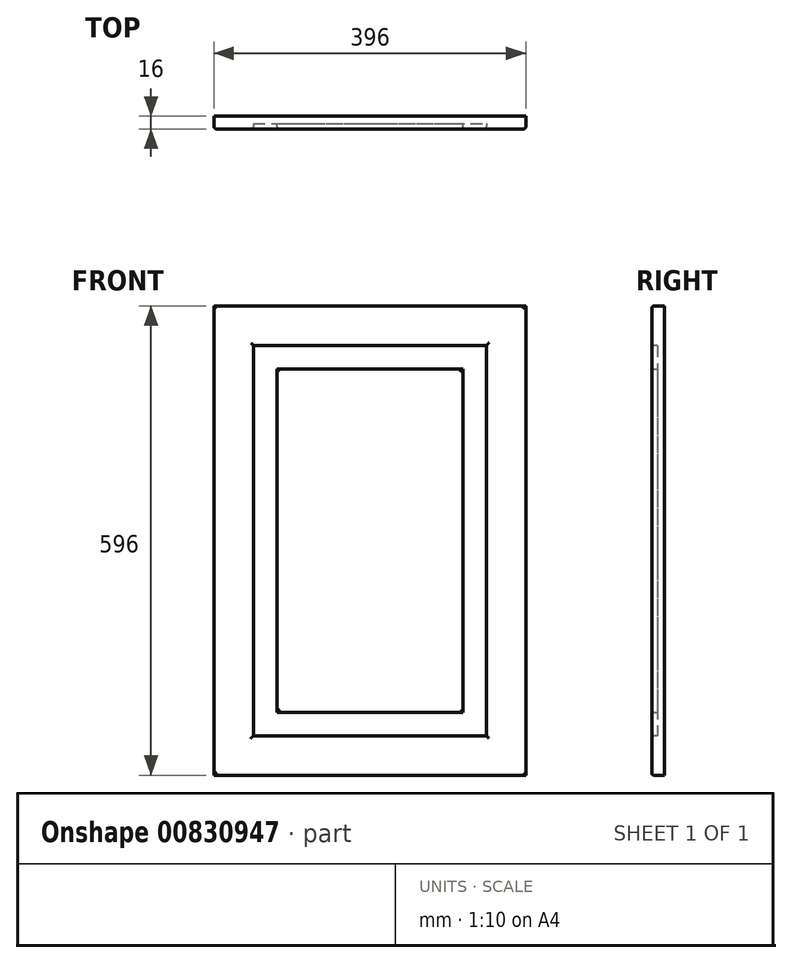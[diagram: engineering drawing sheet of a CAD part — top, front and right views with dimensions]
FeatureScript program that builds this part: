
annotation { "Feature Type Name" : "Feature", "Feature Type Description" : "" }
export const myFeature = defineFeature(function(context is Context, id is Id, definition is map)
    precondition{}
    {
        {
            var Q0;
            Q0=qCreatedBy(makeId("Front.planeOp"),FACE);
            var sketch = newSketch(context, id + "F0", { "sketchPlane" : qUnion([Q0])});
            skLineSegment(sketch, "E0.bottom", {"start": v(0, 0) * mm, "end": v(44.66, 0) * mm});
            skLineSegment(sketch, "E0.top", {"start": v(0, 33.8) * mm, "end": v(44.66, 33.8) * mm});
            skLineSegment(sketch, "E0.left", {"start": v(0, 0) * mm, "end": v(0, 33.8) * mm});
            skLineSegment(sketch, "E0.right", {"start": v(44.66, 0) * mm, "end": v(44.66, 33.8) * mm});
            skSolve(sketch);
        }
        {
            var Q0;
            Q0=makeQuery(id+"F0.imprint","IMPRINT",FACE,{"disambiguationData":[TD([[makeQuery(id+"F0.imprint","IMPRINT",EDGE,{"derivedFrom":sQuery(id+"F0.wireOp",EDGE,"E0.bottom")}),1.0]])]});
            extrude(context, id + "F1", {"entities" : qUnion([Q0]), "depth" : 16 * mm, "offsetDistance" : 25.4 * mm});
        }
        {
            var Q0;
            Q0=makeQuery(id+"F1.opExtrude","SWEPT_FACE",FACE,{"disambiguationData":[OSD([sQuery(id+"F0.wireOp",EDGE,"E0.bottom")])]});
            extrude(context, id + "F2", {"entities" : qUnion([Q0]), "operationType" : NewBodyOperationType.ADD, "oppositeDirection" : true, "depth" : 796 * mm, "offsetDistance" : 25 * mm});
        }
        {
            var Q0;
            {var subQ0=sQuery(id+"F0.wireOp",EDGE,"E0.left");Q0=makeQuery(id+"F2.boolean.opBoolean","MERGE",FACE,{"derivedFrom":[makeQuery(id+"F1.opExtrude","SWEPT_FACE",FACE,{"disambiguationData":[OSD([subQ0])]}),makeQuery(id+"F2.opExtrude","SWEPT_FACE",FACE,{"disambiguationData":[OSD([sQuery(id+"F0.wireOp",EDGE,"E0.bottom"),subQ0])]})]});}
            extrude(context, id + "F3", {"entities" : qUnion([Q0]), "operationType" : NewBodyOperationType.ADD, "oppositeDirection" : true, "depth" : 196 * mm, "offsetDistance" : 25 * mm});
        }
        {
            var Q0;
            {var subQ0=sQuery(id+"F0.wireOp",EDGE,"E0.left");var subQ1=sQuery(id+"F0.wireOp",EDGE,"E0.bottom");Q0=makeQuery(id+"F3.boolean.opBoolean","MERGE",FACE,{"derivedFrom":[makeQuery(id+"F2.boolean.opBoolean","MERGE",FACE,{"derivedFrom":[makeQuery(id+"F1.opExtrude","CAP_FACE",FACE,{"disambiguationData":[OSD([subQ1,sQuery(id+"F0.wireOp",EDGE,"E0.top"),subQ0,sQuery(id+"F0.wireOp",EDGE,"E0.right")])],"isStart":false}),makeQuery(id+"F2.opExtrude","SWEPT_FACE",FACE,{"disambiguationData":[OSD([subQ1]),TDD([makeQuery(id+"F1.opExtrude","CAP_EDGE",EDGE,{"disambiguationData":[OSD([subQ1])],"isStart":false})])]})]}),makeQuery(id+"F3.opExtrude","SWEPT_FACE",FACE,{"disambiguationData":[OSD([subQ1,subQ0]),TDD([makeQuery(id+"F2.boolean.opBoolean","MERGE",EDGE,{"derivedFrom":[makeQuery(id+"F1.opExtrude","CAP_EDGE",EDGE,{"disambiguationData":[OSD([subQ0])],"isStart":false}),makeQuery(id+"F2.opExtrude","SWEPT_EDGE",EDGE,{"disambiguationData":[OSD([subQ1,subQ0]),TDD([makeQuery(id+"F1.opExtrude","CAP_VERTEX",VERTEX,{"disambiguationData":[OSD([subQ1,subQ0])],"isStart":false})])]})]})])]})]});}
            var sketch = newSketch(context, id + "F4", { "sketchPlane" : qUnion([Q0])});
            skLineSegment(sketch, "E1.bottom", {"start": v(59.7, 646.67) * mm, "end": v(128.66, 646.67) * mm});
            skLineSegment(sketch, "E1.top", {"start": v(59.7, 152.97) * mm, "end": v(128.66, 152.97) * mm});
            skLineSegment(sketch, "E1.left", {"start": v(59.7, 646.67) * mm, "end": v(59.7, 152.97) * mm});
            skLineSegment(sketch, "E1.right", {"start": v(128.66, 646.67) * mm, "end": v(128.66, 152.97) * mm});
            skSolve(sketch);
        }
        {
            var Q0;
            Q0=makeQuery(id+"F4.imprint","IMPRINT",FACE,{"disambiguationData":[TD([[makeQuery(id+"F4.imprint","IMPRINT",EDGE,{"derivedFrom":sQuery(id+"F4.wireOp",EDGE,"E1.bottom")}),-1.0]])]});
            extrude(context, id + "F5", {"entities" : qUnion([Q0]), "operationType" : NewBodyOperationType.REMOVE, "oppositeDirection" : true, "depth" : 7 * mm, "offsetDistance" : 25 * mm});
        }
        {
            var Q0;
            Q0=makeQuery(id+"F5.boolean.opBoolean","COPY",FACE,{"derivedFrom":makeQuery(id+"F5.opExtrude","SWEPT_FACE",FACE,{"disambiguationData":[OSD([sQuery(id+"F4.wireOp",EDGE,"E1.left")])]})});
            extrude(context, id + "F6", {"entities" : qUnion([Q0]), "operationType" : NewBodyOperationType.REMOVE, "oppositeDirection" : true, "depth" : 9.7 * mm, "offsetDistance" : 25 * mm});
        }
        {
            var Q0;
            {var subQ0=sQuery(id+"F4.wireOp",EDGE,"E1.bottom");Q0=makeQuery(id+"F6.boolean.opBoolean","MERGE",FACE,{"derivedFrom":[makeQuery(id+"F5.boolean.opBoolean","COPY",FACE,{"derivedFrom":makeQuery(id+"F5.opExtrude","SWEPT_FACE",FACE,{"disambiguationData":[OSD([subQ0])]})}),makeQuery(id+"F6.opExtrude","SWEPT_FACE",FACE,{"disambiguationData":[OSD([subQ0,sQuery(id+"F4.wireOp",EDGE,"E1.left")])]})]});}
            extrude(context, id + "F7", {"entities" : qUnion([Q0]), "operationType" : NewBodyOperationType.ADD, "oppositeDirection" : true, "depth" : 99.33 * mm, "offsetDistance" : 25 * mm});
        }
        {
            var Q0;
            {var subQ0=sQuery(id+"F4.wireOp",EDGE,"E1.bottom");Q0=makeQuery(id+"F6.boolean.opBoolean","MERGE",FACE,{"derivedFrom":[makeQuery(id+"F5.boolean.opBoolean","COPY",FACE,{"derivedFrom":makeQuery(id+"F5.opExtrude","SWEPT_FACE",FACE,{"disambiguationData":[OSD([subQ0])]})}),makeQuery(id+"F6.opExtrude","SWEPT_FACE",FACE,{"disambiguationData":[OSD([subQ0,sQuery(id+"F4.wireOp",EDGE,"E1.left")])]})]});}
            extrude(context, id + "F8", {"entities" : qUnion([Q0]), "operationType" : NewBodyOperationType.REMOVE, "oppositeDirection" : true, "depth" : 99.33 * mm, "offsetDistance" : 25 * mm});
        }
        {
            var Q0;
            {var subQ0=sQuery(id+"F4.wireOp",EDGE,"E1.right");Q0=makeQuery(id+"F8.boolean.opBoolean","MERGE",FACE,{"derivedFrom":[makeQuery(id+"F5.boolean.opBoolean","COPY",FACE,{"derivedFrom":makeQuery(id+"F5.opExtrude","SWEPT_FACE",FACE,{"disambiguationData":[OSD([subQ0])]})}),makeQuery(id+"F8.opExtrude","SWEPT_FACE",FACE,{"disambiguationData":[OSD([sQuery(id+"F4.wireOp",EDGE,"E1.bottom"),subQ0])]})]});}
            extrude(context, id + "F9", {"entities" : qUnion([Q0]), "operationType" : NewBodyOperationType.REMOVE, "oppositeDirection" : true, "depth" : 17.34 * mm, "offsetDistance" : 25 * mm});
        }
        {
            var Q0;
            {var subQ0=sQuery(id+"F4.wireOp",EDGE,"E1.top");Q0=makeQuery(id+"F9.boolean.opBoolean","MERGE",FACE,{"derivedFrom":[makeQuery(id+"F6.boolean.opBoolean","MERGE",FACE,{"derivedFrom":[makeQuery(id+"F5.boolean.opBoolean","COPY",FACE,{"derivedFrom":makeQuery(id+"F5.opExtrude","SWEPT_FACE",FACE,{"disambiguationData":[OSD([subQ0])]})}),makeQuery(id+"F6.opExtrude","SWEPT_FACE",FACE,{"disambiguationData":[OSD([subQ0,sQuery(id+"F4.wireOp",EDGE,"E1.left")])]})]}),makeQuery(id+"F9.opExtrude","SWEPT_FACE",FACE,{"disambiguationData":[OSD([subQ0,sQuery(id+"F4.wireOp",EDGE,"E1.right")])]})]});}
            extrude(context, id + "F10", {"entities" : qUnion([Q0]), "operationType" : NewBodyOperationType.REMOVE, "oppositeDirection" : true, "depth" : 102.97 * mm, "offsetDistance" : 25 * mm});
        }
        {
            var Q0;
            {var subQ0=sQuery(id+"F4.wireOp",EDGE,"E1.right");var subQ1=sQuery(id+"F4.wireOp",EDGE,"E1.top");var subQ2=sQuery(id+"F4.wireOp",EDGE,"E1.left");var subQ3=sQuery(id+"F4.wireOp",EDGE,"E1.bottom");Q0=makeQuery(id+"F10.boolean.opBoolean","MERGE",FACE,{"derivedFrom":[makeQuery(id+"F9.boolean.opBoolean","MERGE",FACE,{"derivedFrom":[makeQuery(id+"F8.boolean.opBoolean","MERGE",FACE,{"derivedFrom":[makeQuery(id+"F6.boolean.opBoolean","MERGE",FACE,{"derivedFrom":[makeQuery(id+"F5.boolean.opBoolean","COPY",FACE,{"derivedFrom":makeQuery(id+"F5.opExtrude","CAP_FACE",FACE,{"disambiguationData":[OSD([subQ3,subQ1,subQ2,subQ0])],"isStart":false})}),makeQuery(id+"F6.opExtrude","SWEPT_FACE",FACE,{"disambiguationData":[OSD([subQ2]),TDD([makeQuery(id+"F5.boolean.opBoolean","COPY",EDGE,{"derivedFrom":makeQuery(id+"F5.opExtrude","CAP_EDGE",EDGE,{"disambiguationData":[OSD([subQ2])],"isStart":false})})])]})]}),makeQuery(id+"F8.opExtrude","SWEPT_FACE",FACE,{"disambiguationData":[OSD([subQ3,subQ2]),TDD([makeQuery(id+"F6.boolean.opBoolean","MERGE",EDGE,{"derivedFrom":[makeQuery(id+"F5.boolean.opBoolean","COPY",EDGE,{"derivedFrom":makeQuery(id+"F5.opExtrude","CAP_EDGE",EDGE,{"disambiguationData":[OSD([subQ3])],"isStart":false})}),makeQuery(id+"F6.opExtrude","SWEPT_EDGE",EDGE,{"disambiguationData":[OSD([subQ3,subQ2]),TDD([makeQuery(id+"F5.boolean.opBoolean","COPY",VERTEX,{"derivedFrom":makeQuery(id+"F5.opExtrude","CAP_VERTEX",VERTEX,{"disambiguationData":[OSD([subQ3,subQ2])],"isStart":false})})])]})]})])]})]}),makeQuery(id+"F9.opExtrude","SWEPT_FACE",FACE,{"disambiguationData":[OSD([subQ3,subQ0]),TDD([makeQuery(id+"F8.boolean.opBoolean","MERGE",EDGE,{"derivedFrom":[makeQuery(id+"F5.boolean.opBoolean","COPY",EDGE,{"derivedFrom":makeQuery(id+"F5.opExtrude","CAP_EDGE",EDGE,{"disambiguationData":[OSD([subQ0])],"isStart":false})}),makeQuery(id+"F8.opExtrude","SWEPT_EDGE",EDGE,{"disambiguationData":[OSD([subQ3,subQ0]),TDD([makeQuery(id+"F5.boolean.opBoolean","COPY",VERTEX,{"derivedFrom":makeQuery(id+"F5.opExtrude","CAP_VERTEX",VERTEX,{"disambiguationData":[OSD([subQ3,subQ0])],"isStart":false})})])]})]})])]})]}),makeQuery(id+"F10.opExtrude","SWEPT_FACE",FACE,{"disambiguationData":[OSD([subQ1,subQ2,subQ0]),TDD([makeQuery(id+"F9.boolean.opBoolean","MERGE",EDGE,{"derivedFrom":[makeQuery(id+"F6.boolean.opBoolean","MERGE",EDGE,{"derivedFrom":[makeQuery(id+"F5.boolean.opBoolean","COPY",EDGE,{"derivedFrom":makeQuery(id+"F5.opExtrude","CAP_EDGE",EDGE,{"disambiguationData":[OSD([subQ1])],"isStart":false})}),makeQuery(id+"F6.opExtrude","SWEPT_EDGE",EDGE,{"disambiguationData":[OSD([subQ1,subQ2]),TDD([makeQuery(id+"F5.boolean.opBoolean","COPY",VERTEX,{"derivedFrom":makeQuery(id+"F5.opExtrude","CAP_VERTEX",VERTEX,{"disambiguationData":[OSD([subQ1,subQ2])],"isStart":false})})])]})]}),makeQuery(id+"F9.opExtrude","SWEPT_EDGE",EDGE,{"disambiguationData":[OSD([subQ1,subQ0]),TDD([makeQuery(id+"F5.boolean.opBoolean","COPY",VERTEX,{"derivedFrom":makeQuery(id+"F5.opExtrude","CAP_VERTEX",VERTEX,{"disambiguationData":[OSD([subQ1,subQ0])],"isStart":false})})])]})]})])]})]});}
            var sketch = newSketch(context, id + "F11", { "sketchPlane" : qUnion([Q0])});
            skLineSegment(sketch, "E2.bottom", {"start": v(74.13, 678.73) * mm, "end": v(109.41, 678.73) * mm});
            skLineSegment(sketch, "E2.top", {"start": v(74.13, 186.63) * mm, "end": v(109.41, 186.63) * mm});
            skLineSegment(sketch, "E2.left", {"start": v(74.13, 678.73) * mm, "end": v(74.13, 186.63) * mm});
            skLineSegment(sketch, "E2.right", {"start": v(109.41, 678.73) * mm, "end": v(109.41, 186.63) * mm});
            skSolve(sketch);
        }
        {
            var Q0;
            Q0=makeQuery(id+"F11.imprint","IMPRINT",FACE,{"disambiguationData":[TD([[makeQuery(id+"F11.imprint","IMPRINT",EDGE,{"derivedFrom":sQuery(id+"F11.wireOp",EDGE,"E2.bottom")}),-1.0]])]});
            extrude(context, id + "F12", {"entities" : qUnion([Q0]), "operationType" : NewBodyOperationType.ADD, "depth" : 7 * mm, "offsetDistance" : 25 * mm});
        }
        {
            var Q0;
            Q0=makeQuery(id+"F12.opExtrude","SWEPT_FACE",FACE,{"disambiguationData":[OSD([sQuery(id+"F11.wireOp",EDGE,"E2.bottom")])]});
            extrude(context, id + "F13", {"entities" : qUnion([Q0]), "operationType" : NewBodyOperationType.ADD, "depth" : 37.27 * mm, "offsetDistance" : 25 * mm});
        }
        {
            var Q0;
            {var subQ0=sQuery(id+"F11.wireOp",EDGE,"E2.right");Q0=makeQuery(id+"F13.boolean.opBoolean","MERGE",FACE,{"derivedFrom":[makeQuery(id+"F12.opExtrude","SWEPT_FACE",FACE,{"disambiguationData":[OSD([subQ0])]}),makeQuery(id+"F13.opExtrude","SWEPT_FACE",FACE,{"disambiguationData":[OSD([sQuery(id+"F11.wireOp",EDGE,"E2.bottom"),subQ0])]})]});}
            extrude(context, id + "F14", {"entities" : qUnion([Q0]), "operationType" : NewBodyOperationType.ADD, "depth" : 6.58 * mm, "offsetDistance" : 25 * mm});
        }
        {
            var Q0;
            {var subQ0=sQuery(id+"F11.wireOp",EDGE,"E2.top");Q0=makeQuery(id+"F14.boolean.opBoolean","MERGE",FACE,{"derivedFrom":[makeQuery(id+"F12.opExtrude","SWEPT_FACE",FACE,{"disambiguationData":[OSD([subQ0])]}),makeQuery(id+"F14.opExtrude","SWEPT_FACE",FACE,{"disambiguationData":[OSD([subQ0,sQuery(id+"F11.wireOp",EDGE,"E2.right")])]})]});}
            extrude(context, id + "F15", {"entities" : qUnion([Q0]), "operationType" : NewBodyOperationType.ADD, "depth" : 106.63 * mm, "offsetDistance" : 25 * mm});
        }
        {
            var Q0;
            {var subQ0=sQuery(id+"F11.wireOp",EDGE,"E2.left");Q0=makeQuery(id+"F15.boolean.opBoolean","MERGE",FACE,{"derivedFrom":[makeQuery(id+"F13.boolean.opBoolean","MERGE",FACE,{"derivedFrom":[makeQuery(id+"F12.opExtrude","SWEPT_FACE",FACE,{"disambiguationData":[OSD([subQ0])]}),makeQuery(id+"F13.opExtrude","SWEPT_FACE",FACE,{"disambiguationData":[OSD([sQuery(id+"F11.wireOp",EDGE,"E2.bottom"),subQ0])]})]}),makeQuery(id+"F15.opExtrude","SWEPT_FACE",FACE,{"disambiguationData":[OSD([sQuery(id+"F11.wireOp",EDGE,"E2.top"),subQ0])]})]});}
            extrude(context, id + "F16", {"entities" : qUnion([Q0]), "operationType" : NewBodyOperationType.REMOVE, "oppositeDirection" : true, "depth" : 5.87 * mm, "offsetDistance" : 25 * mm});
        }
        {
            var Q0;
            Q0=makeQuery(id+"F3.opExtrude","CAP_FACE",FACE,{"disambiguationData":[OSD([sQuery(id+"F0.wireOp",EDGE,"E0.bottom"),sQuery(id+"F0.wireOp",EDGE,"E0.left")])],"isStart":false});
            extrude(context, id + "F17", {"entities" : qUnion([Q0]), "operationType" : NewBodyOperationType.ADD, "depth" : 200 * mm, "offsetDistance" : 25 * mm});
        }
        {
            var Q0;
            {var subQ0=sQuery(id+"F4.wireOp",EDGE,"E1.right");Q0=makeQuery(id+"F10.boolean.opBoolean","MERGE",FACE,{"derivedFrom":[makeQuery(id+"F9.boolean.opBoolean","COPY",FACE,{"derivedFrom":makeQuery(id+"F9.opExtrude","CAP_FACE",FACE,{"disambiguationData":[OSD([sQuery(id+"F4.wireOp",EDGE,"E1.bottom"),subQ0])],"isStart":false})}),makeQuery(id+"F10.opExtrude","SWEPT_FACE",FACE,{"disambiguationData":[OSD([sQuery(id+"F4.wireOp",EDGE,"E1.top"),subQ0])]})]});}
            extrude(context, id + "F18", {"entities" : qUnion([Q0]), "operationType" : NewBodyOperationType.REMOVE, "oppositeDirection" : true, "depth" : 200 * mm, "offsetDistance" : 25 * mm});
        }
        {
            var Q0;
            {var subQ0=sQuery(id+"F11.wireOp",EDGE,"E2.right");var subQ1=sQuery(id+"F11.wireOp",EDGE,"E2.top");Q0=makeQuery(id+"F15.boolean.opBoolean","MERGE",FACE,{"derivedFrom":[makeQuery(id+"F14.opExtrude","CAP_FACE",FACE,{"disambiguationData":[OSD([sQuery(id+"F11.wireOp",EDGE,"E2.bottom"),subQ0])],"isStart":false}),makeQuery(id+"F15.opExtrude","SWEPT_FACE",FACE,{"disambiguationData":[OSD([subQ1,subQ0]),TDD([makeQuery(id+"F14.opExtrude","CAP_EDGE",EDGE,{"disambiguationData":[OSD([subQ1,subQ0])],"isStart":false})])]})]});}
            extrude(context, id + "F19", {"entities" : qUnion([Q0]), "operationType" : NewBodyOperationType.ADD, "depth" : 200 * mm, "offsetDistance" : 25 * mm});
        }
        {
            var Q0;
            {var subQ0=sQuery(id+"F11.wireOp",EDGE,"E2.right");var subQ1=sQuery(id+"F11.wireOp",EDGE,"E2.top");Q0=makeQuery(id+"F19.boolean.opBoolean","MERGE",FACE,{"derivedFrom":[makeQuery(id+"F15.opExtrude","CAP_FACE",FACE,{"disambiguationData":[OSD([subQ1,subQ0])],"isStart":false}),makeQuery(id+"F19.opExtrude","SWEPT_FACE",FACE,{"disambiguationData":[OSD([subQ1,subQ0])]})]});}
            extrude(context, id + "F20", {"entities" : qUnion([Q0]), "operationType" : NewBodyOperationType.REMOVE, "oppositeDirection" : true, "depth" : 600 * mm, "offsetDistance" : 25 * mm});
        }
        {
            var Q0;
            {var subQ0=sQuery(id+"F4.wireOp",EDGE,"E1.right");var subQ1=sQuery(id+"F4.wireOp",EDGE,"E1.top");Q0=makeQuery(id+"F18.boolean.opBoolean","MERGE",FACE,{"derivedFrom":[makeQuery(id+"F10.boolean.opBoolean","COPY",FACE,{"derivedFrom":makeQuery(id+"F10.opExtrude","CAP_FACE",FACE,{"disambiguationData":[OSD([subQ1,sQuery(id+"F4.wireOp",EDGE,"E1.left"),subQ0])],"isStart":false})}),makeQuery(id+"F18.opExtrude","SWEPT_FACE",FACE,{"disambiguationData":[OSD([subQ1,subQ0])]})]});}
            extrude(context, id + "F21", {"entities" : qUnion([Q0]), "operationType" : NewBodyOperationType.ADD, "depth" : 600 * mm, "offsetDistance" : 25 * mm});
        }
        {
            var Q0;
            {var subQ0=sQuery(id+"F0.wireOp",EDGE,"E0.left");var subQ1=sQuery(id+"F0.wireOp",EDGE,"E0.bottom");var subQ2=makeQuery(id+"F1.opExtrude","SWEPT_EDGE",EDGE,{"disambiguationData":[OSD([subQ1,subQ0])]});Q0=makeQuery(id+"F17.boolean.opBoolean","MERGE",FACE,{"derivedFrom":[makeQuery(id+"F3.boolean.opBoolean","MERGE",FACE,{"derivedFrom":[makeQuery(id+"F1.opExtrude","SWEPT_FACE",FACE,{"disambiguationData":[OSD([subQ1])]}),makeQuery(id+"F3.opExtrude","SWEPT_FACE",FACE,{"disambiguationData":[OSD([subQ1,subQ0]),TDD([subQ2])]})]}),makeQuery(id+"F17.opExtrude","SWEPT_FACE",FACE,{"disambiguationData":[OSD([subQ1,subQ0]),TDD([makeQuery(id+"F3.opExtrude","CAP_EDGE",EDGE,{"disambiguationData":[OSD([subQ1,subQ0]),TDD([subQ2])],"isStart":false})])]})]});}
            extrude(context, id + "F22", {"entities" : qUnion([Q0]), "operationType" : NewBodyOperationType.REMOVE, "oppositeDirection" : true, "depth" : 600 * mm, "offsetDistance" : 25 * mm});
        }
        {
            var Q0;
            Q0=makeQuery(id+"F22.boolean.opBoolean","COPY",FACE,{"derivedFrom":makeQuery(id+"F22.opExtrude","CAP_FACE",FACE,{"disambiguationData":[OSD([sQuery(id+"F0.wireOp",EDGE,"E0.bottom"),sQuery(id+"F0.wireOp",EDGE,"E0.left")])],"isStart":false})});
            extrude(context, id + "F23", {"entities" : qUnion([Q0]), "operationType" : NewBodyOperationType.ADD, "depth" : 200 * mm, "offsetDistance" : 25 * mm});
        }
        {
            var Q0;
            Q0=makeQuery(id+"F21.opExtrude","CAP_FACE",FACE,{"disambiguationData":[OSD([sQuery(id+"F4.wireOp",EDGE,"E1.top"),sQuery(id+"F4.wireOp",EDGE,"E1.left"),sQuery(id+"F4.wireOp",EDGE,"E1.right")])],"isStart":false});
            extrude(context, id + "F24", {"entities" : qUnion([Q0]), "operationType" : NewBodyOperationType.REMOVE, "oppositeDirection" : true, "depth" : 200 * mm, "offsetDistance" : 25 * mm});
        }
        {
            var Q0;
            Q0=makeQuery(id+"F20.boolean.opBoolean","COPY",FACE,{"derivedFrom":makeQuery(id+"F20.opExtrude","CAP_FACE",FACE,{"disambiguationData":[OSD([sQuery(id+"F11.wireOp",EDGE,"E2.top"),sQuery(id+"F11.wireOp",EDGE,"E2.right")])],"isStart":false})});
            extrude(context, id + "F25", {"entities" : qUnion([Q0]), "operationType" : NewBodyOperationType.ADD, "depth" : 200 * mm, "offsetDistance" : 25 * mm});
        }
        {
            var Q0;
            {var subQ0=sQuery(id+"F0.wireOp",EDGE,"E0.left");var subQ1=sQuery(id+"F0.wireOp",EDGE,"E0.bottom");var subQ2=makeQuery(id+"F2.opExtrude","CAP_EDGE",EDGE,{"disambiguationData":[OSD([subQ1,subQ0])],"isStart":false});Q0=makeQuery(id+"F17.boolean.opBoolean","MERGE",FACE,{"derivedFrom":[makeQuery(id+"F3.boolean.opBoolean","MERGE",FACE,{"derivedFrom":[makeQuery(id+"F2.opExtrude","CAP_FACE",FACE,{"disambiguationData":[OSD([subQ1])],"isStart":false}),makeQuery(id+"F3.opExtrude","SWEPT_FACE",FACE,{"disambiguationData":[OSD([subQ1,subQ0]),TDD([subQ2])]})]}),makeQuery(id+"F17.opExtrude","SWEPT_FACE",FACE,{"disambiguationData":[OSD([subQ1,subQ0]),TDD([makeQuery(id+"F3.opExtrude","CAP_EDGE",EDGE,{"disambiguationData":[OSD([subQ1,subQ0]),TDD([subQ2])],"isStart":false})])]})]});}
            extrude(context, id + "F26", {"entities" : qUnion([Q0]), "operationType" : NewBodyOperationType.ADD, "depth" : 200 * mm, "offsetDistance" : 25 * mm});
        }
        {
            var Q0;
            {var subQ0=sQuery(id+"F4.wireOp",EDGE,"E1.right");var subQ1=sQuery(id+"F4.wireOp",EDGE,"E1.bottom");Q0=makeQuery(id+"F18.boolean.opBoolean","MERGE",FACE,{"derivedFrom":[makeQuery(id+"F9.boolean.opBoolean","MERGE",FACE,{"derivedFrom":[makeQuery(id+"F8.boolean.opBoolean","COPY",FACE,{"derivedFrom":makeQuery(id+"F8.opExtrude","CAP_FACE",FACE,{"disambiguationData":[OSD([subQ1,sQuery(id+"F4.wireOp",EDGE,"E1.left")])],"isStart":false})}),makeQuery(id+"F9.opExtrude","SWEPT_FACE",FACE,{"disambiguationData":[OSD([subQ1,subQ0]),TDD([makeQuery(id+"F8.boolean.opBoolean","COPY",EDGE,{"derivedFrom":makeQuery(id+"F8.opExtrude","CAP_EDGE",EDGE,{"disambiguationData":[OSD([subQ1,subQ0])],"isStart":false})})])]})]}),makeQuery(id+"F18.opExtrude","SWEPT_FACE",FACE,{"disambiguationData":[OSD([subQ1,subQ0])]})]});}
            extrude(context, id + "F27", {"entities" : qUnion([Q0]), "operationType" : NewBodyOperationType.REMOVE, "oppositeDirection" : true, "depth" : 200 * mm, "offsetDistance" : 25 * mm});
        }
        {
            var Q0;
            {var subQ0=sQuery(id+"F11.wireOp",EDGE,"E2.right");var subQ1=sQuery(id+"F11.wireOp",EDGE,"E2.bottom");Q0=makeQuery(id+"F19.boolean.opBoolean","MERGE",FACE,{"derivedFrom":[makeQuery(id+"F14.boolean.opBoolean","MERGE",FACE,{"derivedFrom":[makeQuery(id+"F13.opExtrude","CAP_FACE",FACE,{"disambiguationData":[OSD([subQ1])],"isStart":false}),makeQuery(id+"F14.opExtrude","SWEPT_FACE",FACE,{"disambiguationData":[OSD([subQ1,subQ0]),TDD([makeQuery(id+"F13.opExtrude","CAP_EDGE",EDGE,{"disambiguationData":[OSD([subQ1,subQ0])],"isStart":false})])]})]}),makeQuery(id+"F19.opExtrude","SWEPT_FACE",FACE,{"disambiguationData":[OSD([subQ1,subQ0])]})]});}
            extrude(context, id + "F28", {"entities" : qUnion([Q0]), "operationType" : NewBodyOperationType.ADD, "depth" : 200 * mm, "offsetDistance" : 25 * mm});
        }
        {
            var Q0;
            {var subQ0=sQuery(id+"F0.wireOp",EDGE,"E0.left");var subQ1=sQuery(id+"F0.wireOp",EDGE,"E0.bottom");var subQ2=makeQuery(id+"F1.opExtrude","CAP_VERTEX",VERTEX,{"disambiguationData":[OSD([subQ1,subQ0])],"isStart":false});var subQ3=makeQuery(id+"F2.opExtrude","CAP_VERTEX",VERTEX,{"disambiguationData":[OSD([subQ1,subQ0]),TDD([subQ2])],"isStart":false});var subQ4=makeQuery(id+"F1.opExtrude","CAP_EDGE",EDGE,{"disambiguationData":[OSD([subQ1])],"isStart":false});var subQ5=sQuery(id+"F4.wireOp",EDGE,"E1.right");var subQ6=sQuery(id+"F4.wireOp",EDGE,"E1.top");var subQ7=makeQuery(id+"F5.boolean.opBoolean","COPY",VERTEX,{"derivedFrom":makeQuery(id+"F5.opExtrude","CAP_VERTEX",VERTEX,{"disambiguationData":[OSD([subQ6,subQ5])],"isStart":true})});var subQ8=sQuery(id+"F4.wireOp",EDGE,"E1.left");var subQ9=makeQuery(id+"F2.boolean.opBoolean","MERGE",EDGE,{"derivedFrom":[makeQuery(id+"F1.opExtrude","CAP_EDGE",EDGE,{"disambiguationData":[OSD([subQ0])],"isStart":false}),makeQuery(id+"F2.opExtrude","SWEPT_EDGE",EDGE,{"disambiguationData":[OSD([subQ1,subQ0]),TDD([subQ2])]})]});Q0=makeQuery(id+"F26.boolean.opBoolean","MERGE",FACE,{"derivedFrom":[makeQuery(id+"F23.boolean.opBoolean","MERGE",FACE,{"derivedFrom":[makeQuery(id+"F21.boolean.opBoolean","MERGE",FACE,{"derivedFrom":[makeQuery(id+"F17.boolean.opBoolean","MERGE",FACE,{"derivedFrom":[makeQuery(id+"F3.boolean.opBoolean","MERGE",FACE,{"derivedFrom":[makeQuery(id+"F2.boolean.opBoolean","MERGE",FACE,{"derivedFrom":[makeQuery(id+"F1.opExtrude","CAP_FACE",FACE,{"disambiguationData":[OSD([subQ1,sQuery(id+"F0.wireOp",EDGE,"E0.top"),subQ0,sQuery(id+"F0.wireOp",EDGE,"E0.right")])],"isStart":false}),makeQuery(id+"F2.opExtrude","SWEPT_FACE",FACE,{"disambiguationData":[OSD([subQ1]),TDD([subQ4])]})]}),makeQuery(id+"F3.opExtrude","SWEPT_FACE",FACE,{"disambiguationData":[OSD([subQ1,subQ0]),TDD([subQ9])]})]}),makeQuery(id+"F17.opExtrude","SWEPT_FACE",FACE,{"disambiguationData":[OSD([subQ1,subQ0]),TDD([makeQuery(id+"F3.opExtrude","CAP_EDGE",EDGE,{"disambiguationData":[OSD([subQ1,subQ0]),TDD([subQ9])],"isStart":false})])]})]}),makeQuery(id+"F21.opExtrude","SWEPT_FACE",FACE,{"disambiguationData":[OSD([subQ6,subQ8,subQ5]),TDD([makeQuery(id+"F18.boolean.opBoolean","MERGE",EDGE,{"derivedFrom":[makeQuery(id+"F10.boolean.opBoolean","COPY",EDGE,{"derivedFrom":makeQuery(id+"F10.opExtrude","CAP_EDGE",EDGE,{"disambiguationData":[OSD([subQ6,subQ8,subQ5]),TDD([makeQuery(id+"F9.boolean.opBoolean","MERGE",EDGE,{"derivedFrom":[makeQuery(id+"F6.boolean.opBoolean","MERGE",EDGE,{"derivedFrom":[makeQuery(id+"F5.boolean.opBoolean","COPY",EDGE,{"derivedFrom":makeQuery(id+"F5.opExtrude","CAP_EDGE",EDGE,{"disambiguationData":[OSD([subQ6])],"isStart":true})}),makeQuery(id+"F6.opExtrude","SWEPT_EDGE",EDGE,{"disambiguationData":[OSD([subQ6,subQ8]),TDD([makeQuery(id+"F5.boolean.opBoolean","COPY",VERTEX,{"derivedFrom":makeQuery(id+"F5.opExtrude","CAP_VERTEX",VERTEX,{"disambiguationData":[OSD([subQ6,subQ8])],"isStart":true})})])]})]}),makeQuery(id+"F9.opExtrude","SWEPT_EDGE",EDGE,{"disambiguationData":[OSD([subQ6,subQ5]),TDD([subQ7])]})]})])],"isStart":false})}),makeQuery(id+"F18.opExtrude","SWEPT_EDGE",EDGE,{"disambiguationData":[OSD([subQ6,subQ5]),TDD([makeQuery(id+"F10.boolean.opBoolean","COPY",VERTEX,{"derivedFrom":makeQuery(id+"F10.opExtrude","CAP_VERTEX",VERTEX,{"disambiguationData":[OSD([subQ6,subQ5]),TDD([makeQuery(id+"F9.boolean.opBoolean","COPY",VERTEX,{"derivedFrom":makeQuery(id+"F9.opExtrude","CAP_VERTEX",VERTEX,{"disambiguationData":[OSD([subQ6,subQ5]),TDD([subQ7])],"isStart":false})})])],"isStart":false})})])]})]})])]})]}),makeQuery(id+"F23.opExtrude","SWEPT_FACE",FACE,{"disambiguationData":[OSD([subQ1,subQ0]),TDD([makeQuery(id+"F22.boolean.opBoolean","COPY",EDGE,{"derivedFrom":makeQuery(id+"F22.opExtrude","CAP_EDGE",EDGE,{"disambiguationData":[OSD([subQ1,subQ0]),TDD([makeQuery(id+"F17.boolean.opBoolean","MERGE",EDGE,{"derivedFrom":[makeQuery(id+"F3.boolean.opBoolean","MERGE",EDGE,{"derivedFrom":[subQ4,makeQuery(id+"F3.opExtrude","SWEPT_EDGE",EDGE,{"disambiguationData":[OSD([subQ1,subQ0]),TDD([subQ2])]})]}),makeQuery(id+"F17.opExtrude","SWEPT_EDGE",EDGE,{"disambiguationData":[OSD([subQ1,subQ0]),TDD([makeQuery(id+"F3.opExtrude","CAP_VERTEX",VERTEX,{"disambiguationData":[OSD([subQ1,subQ0]),TDD([subQ2])],"isStart":false})])]})]})])],"isStart":false})})])]})]}),makeQuery(id+"F26.opExtrude","SWEPT_FACE",FACE,{"disambiguationData":[OSD([subQ1,subQ0]),TDD([makeQuery(id+"F17.boolean.opBoolean","MERGE",EDGE,{"derivedFrom":[makeQuery(id+"F3.boolean.opBoolean","MERGE",EDGE,{"derivedFrom":[makeQuery(id+"F2.opExtrude","CAP_EDGE",EDGE,{"disambiguationData":[OSD([subQ1]),TDD([subQ4])],"isStart":false}),makeQuery(id+"F3.opExtrude","SWEPT_EDGE",EDGE,{"disambiguationData":[OSD([subQ1,subQ0]),TDD([subQ3])]})]}),makeQuery(id+"F17.opExtrude","SWEPT_EDGE",EDGE,{"disambiguationData":[OSD([subQ1,subQ0]),TDD([makeQuery(id+"F3.opExtrude","CAP_VERTEX",VERTEX,{"disambiguationData":[OSD([subQ1,subQ0]),TDD([subQ3])],"isStart":false})])]})]})])]})]});}
            var Q1;
            {var subQ0=sQuery(id+"F11.wireOp",EDGE,"E2.right");var subQ1=sQuery(id+"F11.wireOp",EDGE,"E2.bottom");var subQ2=makeQuery(id+"F12.opExtrude","CAP_VERTEX",VERTEX,{"disambiguationData":[OSD([subQ1,subQ0])],"isStart":false});var subQ3=makeQuery(id+"F13.opExtrude","CAP_VERTEX",VERTEX,{"disambiguationData":[OSD([subQ1,subQ0]),TDD([subQ2])],"isStart":false});var subQ4=makeQuery(id+"F12.opExtrude","CAP_EDGE",EDGE,{"disambiguationData":[OSD([subQ1])],"isStart":false});var subQ5=sQuery(id+"F11.wireOp",EDGE,"E2.top");var subQ6=makeQuery(id+"F12.opExtrude","CAP_VERTEX",VERTEX,{"disambiguationData":[OSD([subQ5,subQ0])],"isStart":false});var subQ7=makeQuery(id+"F14.opExtrude","CAP_VERTEX",VERTEX,{"disambiguationData":[OSD([subQ5,subQ0]),TDD([subQ6])],"isStart":false});var subQ8=makeQuery(id+"F14.boolean.opBoolean","MERGE",EDGE,{"derivedFrom":[makeQuery(id+"F12.opExtrude","CAP_EDGE",EDGE,{"disambiguationData":[OSD([subQ5])],"isStart":false}),makeQuery(id+"F14.opExtrude","SWEPT_EDGE",EDGE,{"disambiguationData":[OSD([subQ5,subQ0]),TDD([subQ6])]})]});var subQ9=makeQuery(id+"F13.boolean.opBoolean","MERGE",EDGE,{"derivedFrom":[makeQuery(id+"F12.opExtrude","CAP_EDGE",EDGE,{"disambiguationData":[OSD([subQ0])],"isStart":false}),makeQuery(id+"F13.opExtrude","SWEPT_EDGE",EDGE,{"disambiguationData":[OSD([subQ1,subQ0]),TDD([subQ2])]})]});Q1=makeQuery(id+"F28.boolean.opBoolean","MERGE",FACE,{"derivedFrom":[makeQuery(id+"F25.boolean.opBoolean","MERGE",FACE,{"derivedFrom":[makeQuery(id+"F19.boolean.opBoolean","MERGE",FACE,{"derivedFrom":[makeQuery(id+"F15.boolean.opBoolean","MERGE",FACE,{"derivedFrom":[makeQuery(id+"F14.boolean.opBoolean","MERGE",FACE,{"derivedFrom":[makeQuery(id+"F13.boolean.opBoolean","MERGE",FACE,{"derivedFrom":[makeQuery(id+"F12.opExtrude","CAP_FACE",FACE,{"disambiguationData":[OSD([subQ1,subQ5,sQuery(id+"F11.wireOp",EDGE,"E2.left"),subQ0])],"isStart":false}),makeQuery(id+"F13.opExtrude","SWEPT_FACE",FACE,{"disambiguationData":[OSD([subQ1]),TDD([subQ4])]})]}),makeQuery(id+"F14.opExtrude","SWEPT_FACE",FACE,{"disambiguationData":[OSD([subQ1,subQ0]),TDD([subQ9])]})]}),makeQuery(id+"F15.opExtrude","SWEPT_FACE",FACE,{"disambiguationData":[OSD([subQ5,subQ0]),TDD([subQ8])]})]}),makeQuery(id+"F19.opExtrude","SWEPT_FACE",FACE,{"disambiguationData":[OSD([subQ1,subQ5,subQ0]),TDD([makeQuery(id+"F15.boolean.opBoolean","MERGE",EDGE,{"derivedFrom":[makeQuery(id+"F14.opExtrude","CAP_EDGE",EDGE,{"disambiguationData":[OSD([subQ1,subQ0]),TDD([subQ9])],"isStart":false}),makeQuery(id+"F15.opExtrude","SWEPT_EDGE",EDGE,{"disambiguationData":[OSD([subQ5,subQ0]),TDD([subQ7])]})]})])]})]}),makeQuery(id+"F25.opExtrude","SWEPT_FACE",FACE,{"disambiguationData":[OSD([subQ5,subQ0]),TDD([makeQuery(id+"F20.boolean.opBoolean","COPY",EDGE,{"derivedFrom":makeQuery(id+"F20.opExtrude","CAP_EDGE",EDGE,{"disambiguationData":[OSD([subQ5,subQ0]),TDD([makeQuery(id+"F19.boolean.opBoolean","MERGE",EDGE,{"derivedFrom":[makeQuery(id+"F15.opExtrude","CAP_EDGE",EDGE,{"disambiguationData":[OSD([subQ5,subQ0]),TDD([subQ8])],"isStart":false}),makeQuery(id+"F19.opExtrude","SWEPT_EDGE",EDGE,{"disambiguationData":[OSD([subQ5,subQ0]),TDD([makeQuery(id+"F15.opExtrude","CAP_VERTEX",VERTEX,{"disambiguationData":[OSD([subQ5,subQ0]),TDD([subQ7])],"isStart":false})])]})]})])],"isStart":false})})])]})]}),makeQuery(id+"F28.opExtrude","SWEPT_FACE",FACE,{"disambiguationData":[OSD([subQ1,subQ0]),TDD([makeQuery(id+"F19.boolean.opBoolean","MERGE",EDGE,{"derivedFrom":[makeQuery(id+"F14.boolean.opBoolean","MERGE",EDGE,{"derivedFrom":[makeQuery(id+"F13.opExtrude","CAP_EDGE",EDGE,{"disambiguationData":[OSD([subQ1]),TDD([subQ4])],"isStart":false}),makeQuery(id+"F14.opExtrude","SWEPT_EDGE",EDGE,{"disambiguationData":[OSD([subQ1,subQ0]),TDD([subQ3])]})]}),makeQuery(id+"F19.opExtrude","SWEPT_EDGE",EDGE,{"disambiguationData":[OSD([subQ1,subQ0]),TDD([makeQuery(id+"F14.opExtrude","CAP_VERTEX",VERTEX,{"disambiguationData":[OSD([subQ1,subQ0]),TDD([subQ3])],"isStart":false})])]})]})])]})]});}
            fillet(context, id + "F29", {"entities" : qUnion([Q0, Q1]), "radius" : 3 * mm, "tangentPropagation" : true, "allowEdgeOverflow" : false});
        }
    });
